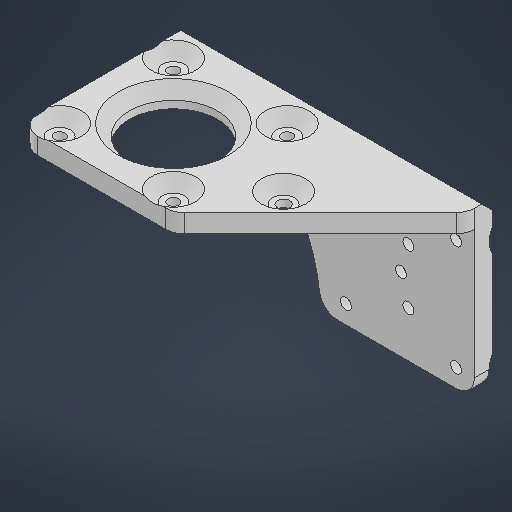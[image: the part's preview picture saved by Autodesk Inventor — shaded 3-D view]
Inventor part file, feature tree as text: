
AUTODESK INVENTOR PART (.ipt)
format: ipt  version: 2025.1 (Build 291241000, 241)  size: 757,248 bytes
history: native  units: mm
features: extrude x7, sketch x4, chamfer x4, fillet x3, projected_geometry x1
ambient origin geometry x8: Origin, YZ Plane, XZ Plane, XY Plane, X Axis, Y Axis, Z Axis, Center Point
bodies: Solid1 (feature_tree)
feature tree (19):
  sketch  "Sketch1"  dims[d0=42.0mm d1=42.0mm d2=31.0mm d3=3.0mm d4=24.0mm d5=40.0mm]
  extrude  "Extrusion1"  Depth=40.0mm
  extrude  "Extrusion2"  Depth=5.0mm TaperAngle=0.0deg
  sketch  "Sketch2"  dims[d6=5.0mm d7=5.0mm d8=0.0mm]
  extrude  "Extrusion3"  TaperAngle=0.0deg  [1 undecoded]
  fillet  "Fillet3"  Radius=20.0mm
  chamfer  "Chamfer3"  Distance=20.0mm
  extrude  "Extrusion4"  Depth=2.0mm
  extrude  "Extrusion5"  Depth=40.0mm
  extrude  "Extrusion6"  Depth=40.0mm TaperAngle=45.0deg
  chamfer  "Chamfer4"  Distance=15.0mm
  extrude  "Extrusion7"  Depth=2.0mm
  chamfer  "Chamfer7"  Distance=18.0mm
  chamfer  "Chamfer6"  Distance=10.0mm
  fillet  "Fillet4"  Radius=6.0mm
  fillet  "Fillet5"  Radius=3.0mm
  sketch  "Sketch3"  dims[d9=40.0mm d10=0.0mm]
  projected_geometry  "Projected Loop1"
  sketch  "Sketch5"  dims[d11=40.0mm d12=40.0mm d13=30.0mm d14=3.0mm d15=3.0mm d16=0.0mm d17=0.0mm d26=20.0mm d27=20.0mm d28=3.4mm d29=40.0mm d30=40.0mm d31=2.0mm d32=45.0deg d33=15.0mm d34=3.0mm d35=18.0mm d36=10.0mm d37=0.0mm d38=6.0mm d39=3.0mm d40=0.0mm d41=6.0mm d42=3.0mm d43=0.0mm d44=3.0mm d45=2.0mm d46=45.0deg d50=3.0mm d51=2.0mm d52=45.0deg d53=5.0mm d54=5.0mm d55=1.0mm d56=10.0mm d57=2.0mm d58=0.0mm d59=1.0mm d60=2.0mm d61=45.0deg d62=5.0mm d63=2.0mm]
note: 1 required parameter value undecoded (feature->parameter linkage not recoverable at this tier; creation-order binding heuristic only, values carry confidence <= 0.55)
